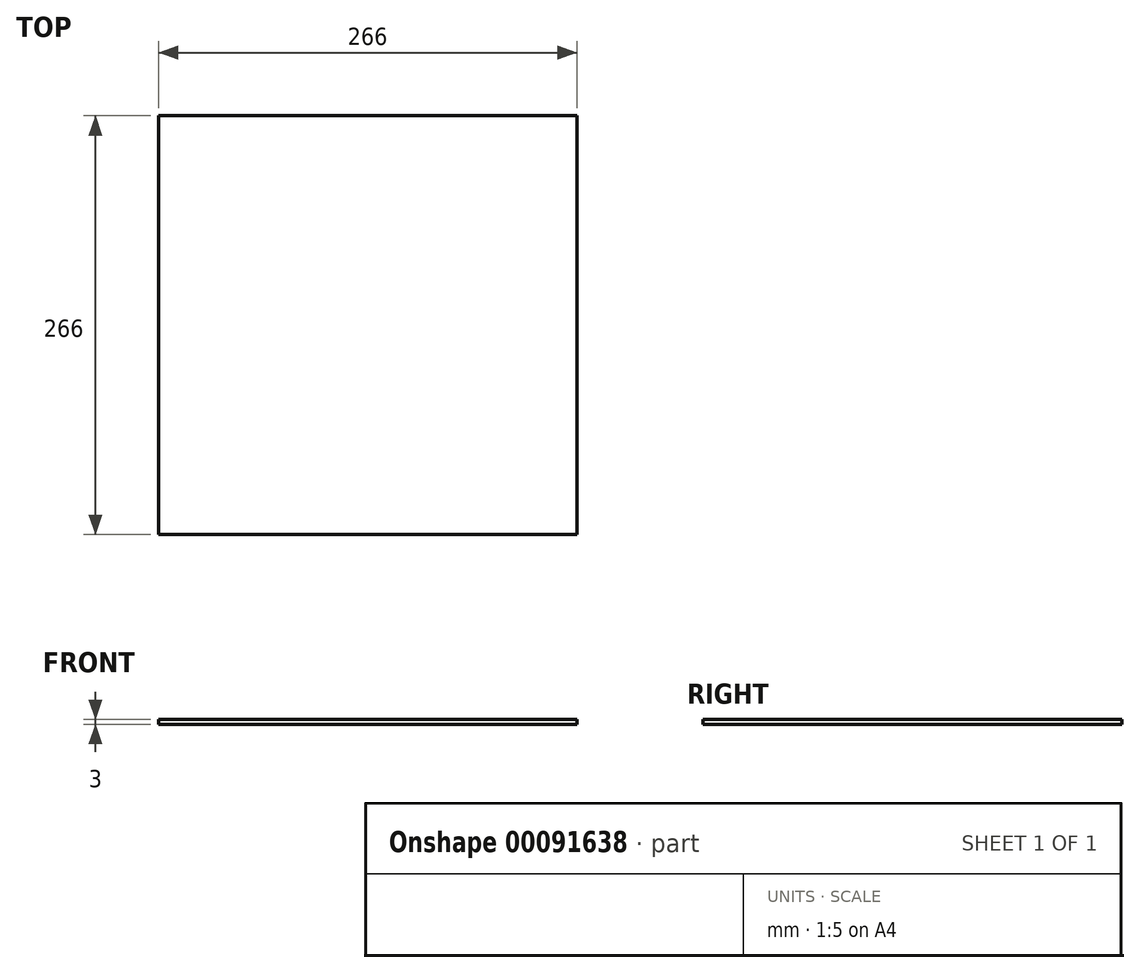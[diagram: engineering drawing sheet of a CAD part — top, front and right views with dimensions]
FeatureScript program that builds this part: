
annotation { "Feature Type Name" : "Feature", "Feature Type Description" : "" }
export const myFeature = defineFeature(function(context is Context, id is Id, definition is map)
    precondition{}
    {
        {
            var Q0;
            Q0=qCreatedBy(makeId("Top.planeOp"),FACE);
            var sketch = newSketch(context, id + "F0", { "sketchPlane" : qUnion([Q0])});
            skLineSegment(sketch, "E0.bottom", {"start": v(133, 133) * mm, "end": v(-133, 133) * mm});
            skLineSegment(sketch, "E0.top", {"start": v(133, -133) * mm, "end": v(-133, -133) * mm});
            skLineSegment(sketch, "E0.left", {"start": v(133, 133) * mm, "end": v(133, -133) * mm});
            skLineSegment(sketch, "E0.right", {"start": v(-133, 133) * mm, "end": v(-133, -133) * mm});
            skPoint(sketch, "E0.middle", {"position": v(0, 0) * mm});
            skSolve(sketch);
        }
        {
            var Q0;
            Q0=makeQuery(id+"F0.imprint","IMPRINT",FACE,{"disambiguationData":[TD([[makeQuery(id+"F0.imprint","IMPRINT",EDGE,{"derivedFrom":sQuery(id+"F0.wireOp",EDGE,"E0.bottom")}),1.0]])]});
            extrude(context, id + "F1", {"entities" : qUnion([Q0]), "depth" : 3 * mm});
        }
    });
